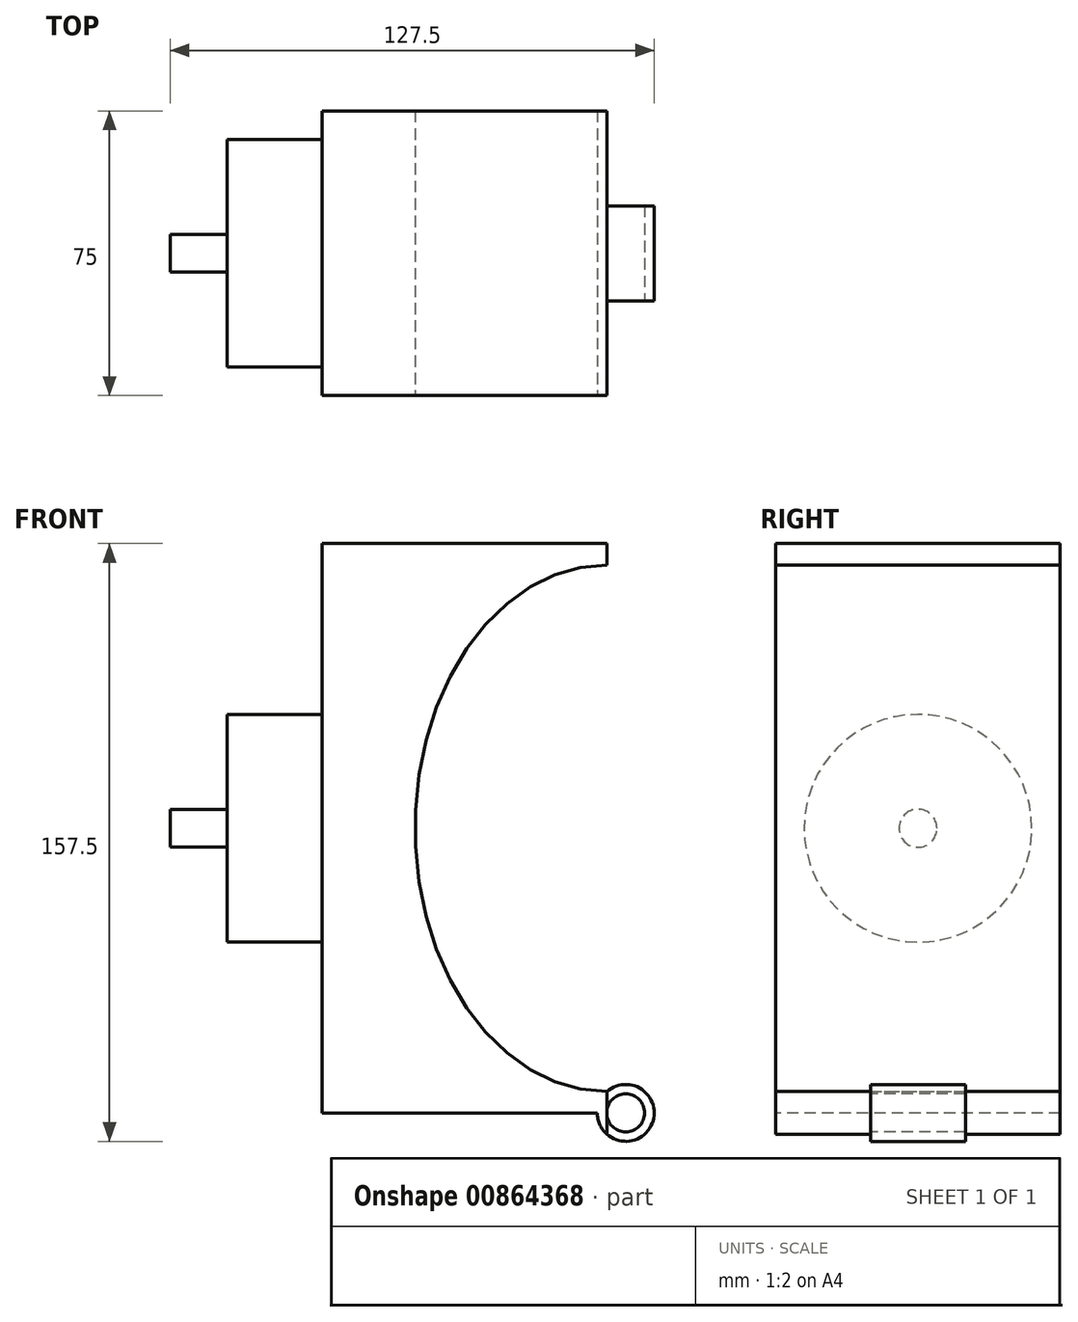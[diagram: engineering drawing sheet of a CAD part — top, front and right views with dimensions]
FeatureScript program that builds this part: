
annotation { "Feature Type Name" : "Feature", "Feature Type Description" : "" }
export const myFeature = defineFeature(function(context is Context, id is Id, definition is map)
    precondition{}
    {
        {
            var Q0;
            Q0=qCreatedBy(makeId("Front.planeOp"),FACE);
            var sketch = newSketch(context, id + "F0", { "sketchPlane" : qUnion([Q0])});
            skLineSegment(sketch, "E0.bottom", {"start": v(75, -75) * mm, "end": v(-75, -75) * mm});
            skLineSegment(sketch, "E0.top", {"start": v(75, 75) * mm, "end": v(-75, 75) * mm});
            skLineSegment(sketch, "E0.left", {"start": v(75, -75) * mm, "end": v(75, 75) * mm});
            skLineSegment(sketch, "E0.right", {"start": v(-75, -75) * mm, "end": v(-75, 75) * mm});
            skPoint(sketch, "E0.middle", {"position": v(0, 0) * mm});
            skEllipse(sketch, "E1", {"center": v(0, 0) * mm, "majorRadius": 69.33 * mm, "minorRadius": 50.52 * mm, "majorAxis": v(0, -1)});
            skLineSegment(sketch, "E2", {"start": v(0, 75) * mm, "end": v(0, -75) * mm});
            skSolve(sketch);
        }
        {
            var Q0;
            {var subQ4=sQuery(id+"F0.wireOp",EDGE,"E0.right");Q0=makeQuery(id+"F0.imprint","IMPRINT",FACE,{"disambiguationData":[TD([[makeQuery(id+"F0.imprint","IMPRINT",EDGE,{"derivedFrom":subQ4}),-1.0]])]});}
            extrude(context, id + "F1", {"entities" : qUnion([Q0]), "depth" : 75 * mm, "offsetDistance" : 25 * mm});
        }
        {
            var Q0;
            Q0=makeQuery(id+"F1.opExtrude","SWEPT_FACE",FACE,{"disambiguationData":[OSD([sQuery(id+"F0.wireOp",EDGE,"E0.right")])]});
            var sketch = newSketch(context, id + "F2", { "sketchPlane" : qUnion([Q0])});
            skCircle(sketch, "E3", {"center": v(37.5, 0) * mm, "radius": 30 * mm});
            skSolve(sketch);
        }
        {
            var Q0;
            Q0=makeQuery(id+"F2.imprint","IMPRINT",FACE,{"disambiguationData":[TD([[makeQuery(id+"F2.imprint","IMPRINT",EDGE,{"derivedFrom":sQuery(id+"F2.wireOp",EDGE,"E3")}),1.0]])]});
            extrude(context, id + "F3", {"entities" : qUnion([Q0]), "operationType" : NewBodyOperationType.ADD, "depth" : 25 * mm, "offsetDistance" : 25 * mm});
        }
        {
            var Q0;
            Q0=makeQuery(id+"F3.opExtrude","CAP_FACE",FACE,{"disambiguationData":[OSD([sQuery(id+"F2.wireOp",EDGE,"E3")])],"isStart":false});
            var sketch = newSketch(context, id + "F4", { "sketchPlane" : qUnion([Q0])});
            skCircle(sketch, "E4", {"center": v(37.5, 0) * mm, "radius": 5 * mm});
            skSolve(sketch);
        }
        {
            var Q0;
            Q0=makeQuery(id+"F4.imprint","IMPRINT",FACE,{"disambiguationData":[TD([[makeQuery(id+"F4.imprint","IMPRINT",EDGE,{"derivedFrom":sQuery(id+"F4.wireOp",EDGE,"E4")}),1.0]])]});
            extrude(context, id + "F5", {"entities" : qUnion([Q0]), "operationType" : NewBodyOperationType.ADD, "depth" : 15 * mm, "offsetDistance" : 25 * mm});
        }
        {
            var Q0;
            Q0=makeQuery(id+"F1.opExtrude","CAP_FACE",FACE,{"disambiguationData":[OSD([sQuery(id+"F0.wireOp",EDGE,"E0.bottom"),sQuery(id+"F0.wireOp",EDGE,"E0.top"),sQuery(id+"F0.wireOp",EDGE,"E0.right"),sQuery(id+"F0.wireOp",EDGE,"E1"),sQuery(id+"F0.wireOp",EDGE,"E2")])],"isStart":false});
            var sketch = newSketch(context, id + "F6", { "sketchPlane" : qUnion([Q0])});
            skCircle(sketch, "E5", {"center": v(5, -75) * mm, "radius": 7.5 * mm});
            skSolve(sketch);
        }
        {
            var Q0;
            {var subQ7=sQuery(id+"F6.wireOp",EDGE,"6TEUvOMH-QbkO-FRns-KI3P-UGPVtDWprrh9");Q0=makeQuery(id+"F6.imprint","IMPRINT",FACE,{"disambiguationData":[TD([[makeQuery(id+"F6.imprint","IMPRINT",EDGE,{"derivedFrom":subQ7}),-1.0]])]});}
            var Q1;
            {var subQ0=sQuery(id+"F6.wireOp",EDGE,"E5");var subQ1=sQuery(id+"F0.wireOp",EDGE,"E0.bottom");var subQ2=makeQuery(id+"F1.opExtrude","CAP_EDGE",EDGE,{"disambiguationData":[OSD([subQ1])],"isStart":false});var subQ3=makeQuery(id+"F6.imprint","INTERSECT",VERTEX,{"derivedFrom":[subQ2,subQ0]});Q1=makeQuery(id+"F6.imprint","IMPRINT",FACE,{"disambiguationData":[TD([[makeQuery(id+"F6.imprint","IMPRINT",EDGE,{"disambiguationData":[TD([[subQ3,-1.0]])],"derivedFrom":subQ0}),1.0]])]});}
            extrude(context, id + "F7", {"entities" : qUnion([Q0, Q1]), "operationType" : NewBodyOperationType.ADD, "oppositeDirection" : true, "depth" : 75 * mm, "offsetDistance" : 25 * mm});
        }
        {
            var Q0;
            {var subQ0=sQuery(id+"F0.wireOp",EDGE,"E2");var subQ1=sQuery(id+"F0.wireOp",EDGE,"E0.bottom");Q0=makeQuery(id+"F7.boolean.opBoolean","MERGE",FACE,{"derivedFrom":[makeQuery(id+"F1.opExtrude","CAP_FACE",FACE,{"disambiguationData":[OSD([subQ1,sQuery(id+"F0.wireOp",EDGE,"E0.top"),sQuery(id+"F0.wireOp",EDGE,"E0.right"),sQuery(id+"F0.wireOp",EDGE,"E1"),subQ0])],"isStart":false}),makeQuery(id+"F7.opExtrude","CAP_FACE",FACE,{"disambiguationData":[OSD([subQ1,subQ0,sQuery(id+"F6.wireOp",EDGE,"E5")])],"isStart":true})]});}
            var sketch = newSketch(context, id + "F8", { "sketchPlane" : qUnion([Q0])});
            skCircle(sketch, "E6", {"center": v(5, -75) * mm, "radius": 5 * mm});
            skSolve(sketch);
        }
        {
            var Q0;
            Q0=makeQuery(id+"F8.imprint","IMPRINT",FACE,{"disambiguationData":[TD([[makeQuery(id+"F8.imprint","IMPRINT",EDGE,{"derivedFrom":sQuery(id+"F8.wireOp",EDGE,"E6")}),1.0]])]});
            extrude(context, id + "F9", {"entities" : qUnion([Q0]), "operationType" : NewBodyOperationType.REMOVE, "oppositeDirection" : true, "depth" : 75 * mm, "offsetDistance" : 25 * mm});
        }
        {
            var Q0;
            Q0=qCreatedBy(makeId("Right.planeOp"),FACE);
            var sketch = newSketch(context, id + "F10", { "sketchPlane" : qUnion([Q0])});
            skLineSegment(sketch, "E7.bottom", {"start": v(-75, -55.82) * mm, "end": v(-50, -55.82) * mm});
            skLineSegment(sketch, "E7.top", {"start": v(-75, -101.1) * mm, "end": v(-50, -101.1) * mm});
            skLineSegment(sketch, "E7.left", {"start": v(-75, -55.82) * mm, "end": v(-75, -101.1) * mm});
            skLineSegment(sketch, "E7.right", {"start": v(-50, -55.82) * mm, "end": v(-50, -101.1) * mm});
            skLineSegment(sketch, "E8.bottom", {"start": v(-25, -56.92) * mm, "end": v(9.9, -56.92) * mm});
            skLineSegment(sketch, "E8.top", {"start": v(-25, -113.53) * mm, "end": v(9.9, -113.53) * mm});
            skLineSegment(sketch, "E8.left", {"start": v(-25, -56.92) * mm, "end": v(-25, -113.53) * mm});
            skLineSegment(sketch, "E8.right", {"start": v(9.9, -56.92) * mm, "end": v(9.9, -113.53) * mm});
            skSolve(sketch);
        }
        {
            var Q0;
            Q0=makeQuery(id+"F10.imprint","IMPRINT",FACE,{"disambiguationData":[TD([[makeQuery(id+"F10.imprint","IMPRINT",EDGE,{"derivedFrom":sQuery(id+"F10.wireOp",EDGE,"E7.bottom")}),-1.0]])]});
            var Q1;
            Q1=makeQuery(id+"F10.imprint","IMPRINT",FACE,{"disambiguationData":[TD([[makeQuery(id+"F10.imprint","IMPRINT",EDGE,{"derivedFrom":sQuery(id+"F10.wireOp",EDGE,"E8.bottom")}),-1.0]])]});
            extrude(context, id + "F11", {"entities" : qUnion([Q0, Q1]), "operationType" : NewBodyOperationType.REMOVE, "depth" : 25 * mm, "offsetDistance" : 25 * mm});
        }
    });
